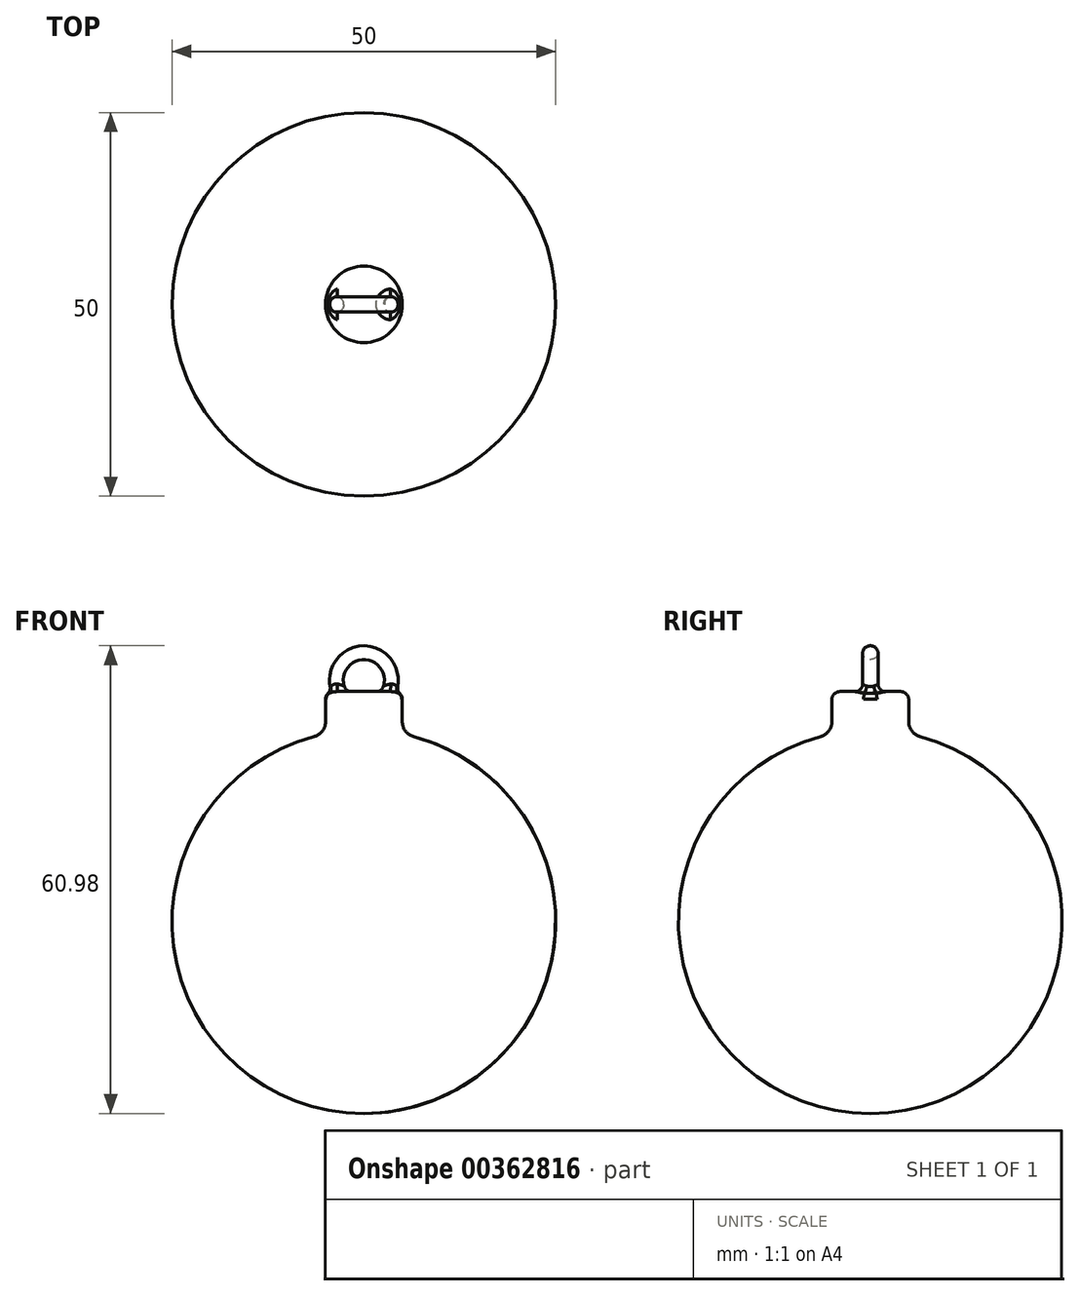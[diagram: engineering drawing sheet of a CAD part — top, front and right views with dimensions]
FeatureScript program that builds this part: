
annotation { "Feature Type Name" : "Feature", "Feature Type Description" : "" }
export const myFeature = defineFeature(function(context is Context, id is Id, definition is map)
    precondition{}
    {
        {
            var Q0;
            Q0=qCreatedBy(makeId("Front.planeOp"),FACE);
            var sketch = newSketch(context, id + "F0", { "sketchPlane" : qUnion([Q0])});
            skCircle(sketch, "E0", {"center": v(0, 0) * mm, "radius": 25 * mm});
            skLineSegment(sketch, "E1", {"start": v(0, 52.03) * mm, "end": v(0, -57.17) * mm});
            skSolve(sketch);
        }
        {
            var Q0;
            {var subQ0=sQuery(id+"F0.wireOp",EDGE,"E1");var subQ1=sQuery(id+"F0.wireOp",EDGE,"E0");var subQ2=makeQuery(id+"F0.imprint","INTERSECT",VERTEX,{"disambiguationData":[OD(0.0)],"derivedFrom":[subQ1,subQ0]});Q0=makeQuery(id+"F0.imprint","IMPRINT",FACE,{"disambiguationData":[TD([[makeQuery(id+"F0.imprint","IMPRINT",EDGE,{"disambiguationData":[TD([[subQ2,1.0]])],"derivedFrom":subQ1}),1.0]])]});}
            var Q1;
            Q1=sQuery(id+"F0.wireOp",EDGE,"E0");
            var Q2;
            Q2=sQuery(id+"F0.wireOp",EDGE,"E1");
            revolve(context, id + "F1", {"entities" : qUnion([Q0]), "surfaceEntities" : qUnion([Q1]), "axis" : qUnion([Q2]), "revolveType" : RevolveType.FULL});
        }
        {
            var Q0;
            Q0=qCreatedBy(makeId("Top.planeOp"),FACE);
            var sketch = newSketch(context, id + "F2", { "sketchPlane" : qUnion([Q0])});
            skCircle(sketch, "E2", {"center": v(0, 0) * mm, "radius": 5 * mm});
            skSolve(sketch);
        }
        {
            var Q0;
            Q0 = qSketchRegion(id + "F2", true);
            extrude(context, id + "F3", {"entities" : qUnion([Q0]), "operationType" : NewBodyOperationType.ADD, "depth" : 30 * mm});
        }
        {
            var Q0;
            Q0=qCreatedBy(makeId("Front.planeOp"),FACE);
            var sketch = newSketch(context, id + "F4", { "sketchPlane" : qUnion([Q0])});
            skCircle(sketch, "E3", {"center": v(0, 31.5) * mm, "radius": 3.25 * mm});
            skSolve(sketch);
        }
        {
            var Q0;
            Q0=makeQuery(id+"F3.opExtrude","CAP_FACE",FACE,{"disambiguationData":[OSD([sQuery(id+"F2.wireOp",EDGE,"E2")])],"isStart":false});
            var sketch = newSketch(context, id + "F5", { "sketchPlane" : qUnion([Q0])});
            skCircle(sketch, "E4", {"center": v(-3.22, 0) * mm, "radius": 1 * mm});
            skSolve(sketch);
        }
        {
            var Q0;
            Q0=makeQuery(id+"F5.imprint","IMPRINT",FACE,{"disambiguationData":[TD([[makeQuery(id+"F5.imprint","IMPRINT",EDGE,{"derivedFrom":sQuery(id+"F5.wireOp",EDGE,"E4")}),1.0]])]});
            var Q1;
            Q1=sQuery(id+"F4.wireOp",EDGE,"E3");
            sweep(context, id + "F6", {"operationType" : NewBodyOperationType.ADD, "profiles" : qUnion([Q0]), "path" : qUnion([Q1])});
        }
        {
            var Q0;
            Q0=makeQuery(id+"F3.boolean.opBoolean","INTERSECT",EDGE,{"derivedFrom":[makeQuery(id+"F1.opRevolve","SWEPT_FACE",FACE,{"disambiguationData":[OSD([sQuery(id+"F0.wireOp",EDGE,"E0")])]}),makeQuery(id+"F3.opExtrude","SWEPT_FACE",FACE,{"disambiguationData":[OSD([sQuery(id+"F2.wireOp",EDGE,"E2")])]})]});
            fillet(context, id + "F7", {"entities" : qUnion([Q0]), "radius" : 2 * mm, "tangentPropagation" : true, "allowEdgeOverflow" : false});
        }
        {
            var Q0;
            Q0=makeQuery(id+"F3.opExtrude","CAP_EDGE",EDGE,{"disambiguationData":[OSD([sQuery(id+"F2.wireOp",EDGE,"E2")])],"isStart":false});
            fillet(context, id + "F8", {"entities" : qUnion([Q0]), "radius" : 1 * mm, "tangentPropagation" : true, "allowEdgeOverflow" : false});
        }
        {
            var Q0;
            Q0=makeQuery(id+"F6.boolean.opBoolean","INTERSECT",EDGE,{"disambiguationData":[OD(0.0)],"derivedFrom":[makeQuery(id+"F3.opExtrude","CAP_FACE",FACE,{"disambiguationData":[OSD([sQuery(id+"F2.wireOp",EDGE,"E2")])],"isStart":false}),makeQuery(id+"F6.opSweep","SWEPT_FACE",FACE,{"disambiguationData":[OSD([sQuery(id+"F4.wireOp",EDGE,"E3"),sQuery(id+"F5.wireOp",EDGE,"E4")])]})]});
            var Q1;
            Q1=makeQuery(id+"F6.boolean.opBoolean","INTERSECT",EDGE,{"disambiguationData":[OD(1.0)],"derivedFrom":[makeQuery(id+"F3.opExtrude","CAP_FACE",FACE,{"disambiguationData":[OSD([sQuery(id+"F2.wireOp",EDGE,"E2")])],"isStart":false}),makeQuery(id+"F6.opSweep","SWEPT_FACE",FACE,{"disambiguationData":[OSD([sQuery(id+"F4.wireOp",EDGE,"E3"),sQuery(id+"F5.wireOp",EDGE,"E4")])]})]});
            fillet(context, id + "F9", {"entities" : qUnion([Q0, Q1]), "radius" : 1 * mm, "tangentPropagation" : true, "allowEdgeOverflow" : false});
        }
    });
